# Revit family: IS_Tesi_A6754_BIM_DE
name_source: partatom
category: Plumbing Fixtures
revit_build: Autodesk Revit 2015 (Build: 20140606_1530(x64)
units: mm (PartAtom-declared; Revit-internal decimal feet)

## types (2) — shared parameters
Accessories = www.idealspec.co.uk
AreaUnits = millimeters
Assembly Code = C1030200
AssetType = Fixed
BIMObjectName = ISI_IdealStandard_WashbasinTaps_Tesi_A6754
BarCode = 4015413339476
Brand = Ideal Standard
Color = Chromium Plated
ConnectionType = Plumbing
Description = TESI BSN MXR RMTD HGH/SPT/SWVL 5L/M PU/M
DurationUnit = year
Features = TESI BSN MXR RMTD HGH/SPT/SWVL 5L/M PU/M
Finish = Chromium Plated
Help = www.idealstandard.de
IfcExportAs = IfcValveType
IfcExportType = BASIN MIXER
InstallationInstructions = www.idealstandard.de
LinearUnits = millimeters
MainColor = Chromium Plated
MaintenanceInformation = www.idealstandard.de
Manufacturer = www.idealstandard.de
ManufacturerURL = www.idealstandard.de
Model = A6754AA
ModelNumber = A6754AA
ModelReference = TESI BSN MXR RMTD HGH/SPT/SWVL 5L/M PU/M
Name = WashbasinTaps_Tesi_A6754_ISI
NettWeight = 3,14 KG
NominalDepth = 405 mm
NominalHeight = 90 mm
NominalLength = 405 mm
NominalWidth = 215 mm
ProductInformation = www.idealstandard.de
Shape = Sculptured
Size = 90 x 405 x 215 mm
Space = Internal
SpareParts = www.idealstandard.de
TestPressure = 10 bar
URL = www.idealstandard.de
Uniclass2015Code = Pr_40_20_87_98
Uniclass2015Title = Washbasin taps
Uniclass2015Version = Products v1.1
zero-valued in all types: Cost

## type names (no varying parameters)
- A6754AA 1
- A6754AA

## geometry (parser evidence)
native form markers: Blend x4
no freeform markers — native parametric forms only
